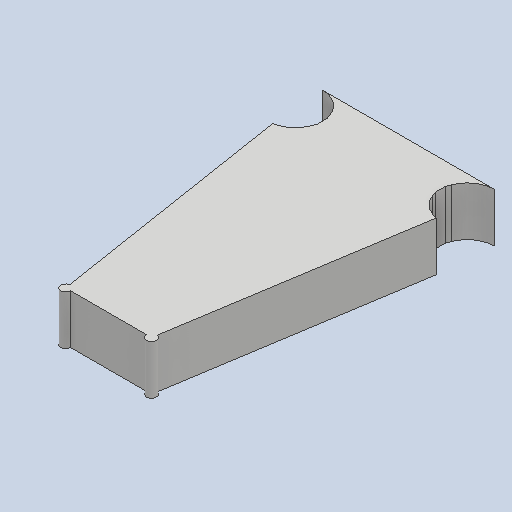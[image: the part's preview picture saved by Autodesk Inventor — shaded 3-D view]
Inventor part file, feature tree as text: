
AUTODESK INVENTOR PART (.ipt)
format: ipt  version: 2024.2 (Build 282272000, 272)  size: 122,368 bytes
history: native  units: mm
features: other x1, extrude x1, sketch x1
ambient origin geometry x8: Origin, YZ Plane, XZ Plane, XY Plane, X Axis, Y Axis, Z Axis, Center Point
bodies: Body1 (feature_tree)
feature tree (3):
  other  "Твердое тело1"
  extrude  "Выдавливание1"  Depth=90.0mm
  sketch  "Эскиз1"
